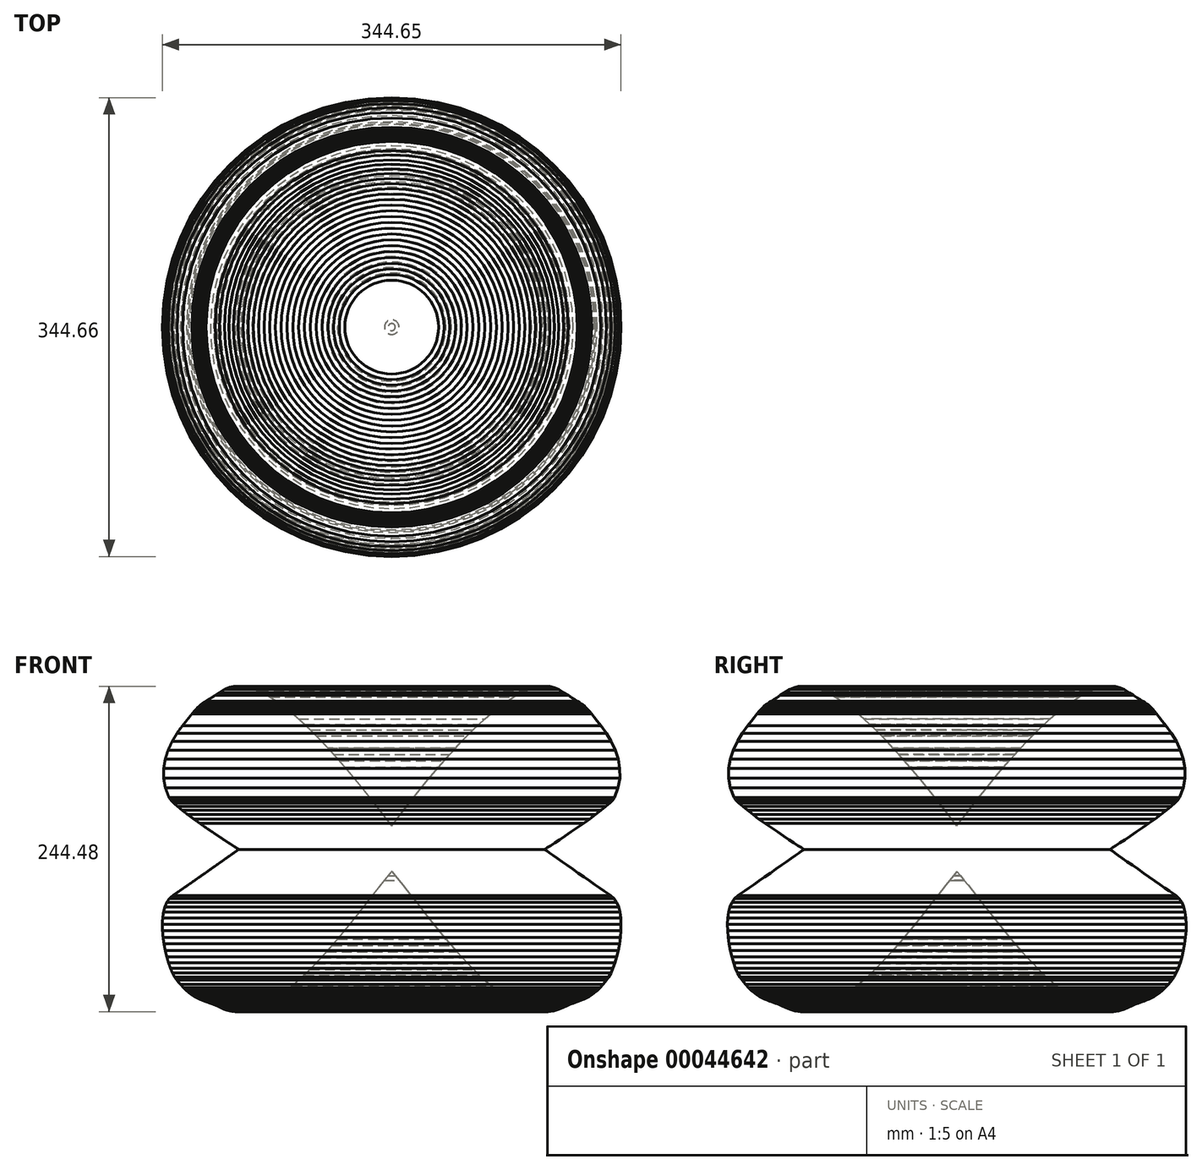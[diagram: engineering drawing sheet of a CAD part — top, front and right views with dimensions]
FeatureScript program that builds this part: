
annotation { "Feature Type Name" : "Feature", "Feature Type Description" : "" }
export const myFeature = defineFeature(function(context is Context, id is Id, definition is map)
    precondition{}
    {
        {
            var Q0;
            Q0=qCreatedBy(makeId("Front.planeOp"),FACE);
            var sketch = newSketch(context, id + "F0", { "sketchPlane" : qUnion([Q0])});
            skLineSegment(sketch, "E0", {"start": v(-86.16, 17.32) * mm, "end": v(-83.34, 21.03) * mm});
            skLineSegment(sketch, "E1", {"start": v(-83.34, 21.03) * mm, "end": v(-80.33, 24.97) * mm});
            skLineSegment(sketch, "E2", {"start": v(-80.33, 24.97) * mm, "end": v(-77.15, 29.11) * mm});
            skLineSegment(sketch, "E3", {"start": v(-77.15, 29.11) * mm, "end": v(-73.8, 33.43) * mm});
            skLineSegment(sketch, "E4", {"start": v(-73.8, 33.43) * mm, "end": v(-70.3, 37.9) * mm});
            skLineSegment(sketch, "E5", {"start": v(-70.3, 37.9) * mm, "end": v(-66.66, 42.47) * mm});
            skLineSegment(sketch, "E6", {"start": v(-66.66, 42.47) * mm, "end": v(-62.9, 47.16) * mm});
            skLineSegment(sketch, "E7", {"start": v(-62.9, 47.16) * mm, "end": v(-59, 51.9) * mm});
            skLineSegment(sketch, "E8", {"start": v(-59, 51.9) * mm, "end": v(-55.02, 56.7) * mm});
            skLineSegment(sketch, "E9", {"start": v(-55.02, 56.7) * mm, "end": v(-50.93, 61.52) * mm});
            skLineSegment(sketch, "E10", {"start": v(-50.93, 61.52) * mm, "end": v(-46.76, 66.33) * mm});
            skLineSegment(sketch, "E11", {"start": v(-46.76, 66.33) * mm, "end": v(-42.52, 71.1) * mm});
            skLineSegment(sketch, "E12", {"start": v(-42.52, 71.1) * mm, "end": v(-38.22, 75.82) * mm});
            skLineSegment(sketch, "E13", {"start": v(-38.22, 75.82) * mm, "end": v(-33.87, 80.45) * mm});
            skLineSegment(sketch, "E14", {"start": v(-33.87, 80.45) * mm, "end": v(-29.49, 84.97) * mm});
            skLineSegment(sketch, "E15", {"start": v(-29.49, 84.97) * mm, "end": v(-25.08, 89.36) * mm});
            skLineSegment(sketch, "E16", {"start": v(-25.08, 89.36) * mm, "end": v(-20.66, 93.58) * mm});
            skLineSegment(sketch, "E17", {"start": v(-20.66, 93.58) * mm, "end": v(-16.23, 97.62) * mm});
            skLineSegment(sketch, "E18", {"start": v(-16.23, 97.62) * mm, "end": v(-11.82, 101.44) * mm});
            skLineSegment(sketch, "E19", {"start": v(-11.82, 101.44) * mm, "end": v(-7.42, 105.03) * mm});
            skLineSegment(sketch, "E20", {"start": v(-7.42, 105.03) * mm, "end": v(-3.06, 108.35) * mm});
            skLineSegment(sketch, "E21", {"start": v(-3.06, 108.35) * mm, "end": v(1.26, 111.37) * mm});
            skLineSegment(sketch, "E22", {"start": v(1.26, 111.37) * mm, "end": v(5.52, 114.08) * mm});
            skLineSegment(sketch, "E23", {"start": v(5.52, 114.08) * mm, "end": v(9.71, 116.45) * mm});
            skLineSegment(sketch, "E24", {"start": v(9.71, 116.45) * mm, "end": v(13.83, 118.45) * mm});
            skLineSegment(sketch, "E25", {"start": v(13.83, 118.45) * mm, "end": v(17.85, 120.05) * mm});
            skLineSegment(sketch, "E26", {"start": v(17.85, 120.05) * mm, "end": v(21.77, 121.24) * mm});
            skLineSegment(sketch, "E27", {"start": v(21.77, 121.24) * mm, "end": v(25.58, 121.97) * mm});
            skLineSegment(sketch, "E28", {"start": v(25.58, 121.97) * mm, "end": v(29.27, 122.24) * mm});
            skLineSegment(sketch, "E29", {"start": v(29.27, 122.24) * mm, "end": v(32.81, 122) * mm});
            skLineSegment(sketch, "E30", {"start": v(32.81, 122) * mm, "end": v(36.21, 121.25) * mm});
            skLineSegment(sketch, "E31", {"start": v(36.21, 121.25) * mm, "end": v(39.45, 119.95) * mm});
            skLineSegment(sketch, "E32", {"start": v(39.45, 119.95) * mm, "end": v(43.29, 117.43) * mm});
            skLineSegment(sketch, "E33", {"start": v(43.29, 117.43) * mm, "end": v(46.52, 115.36) * mm});
            skLineSegment(sketch, "E34", {"start": v(46.52, 115.36) * mm, "end": v(49.22, 113.67) * mm});
            skLineSegment(sketch, "E35", {"start": v(49.22, 113.67) * mm, "end": v(51.47, 112.28) * mm});
            skLineSegment(sketch, "E36", {"start": v(51.47, 112.28) * mm, "end": v(53.35, 111.13) * mm});
            skLineSegment(sketch, "E37", {"start": v(53.35, 111.13) * mm, "end": v(54.92, 110.13) * mm});
            skLineSegment(sketch, "E38", {"start": v(54.92, 110.13) * mm, "end": v(56.28, 109.22) * mm});
            skLineSegment(sketch, "E39", {"start": v(56.28, 109.22) * mm, "end": v(57.48, 108.32) * mm});
            skLineSegment(sketch, "E40", {"start": v(57.48, 108.32) * mm, "end": v(58.62, 107.36) * mm});
            skLineSegment(sketch, "E41", {"start": v(58.62, 107.36) * mm, "end": v(59.76, 106.26) * mm});
            skLineSegment(sketch, "E42", {"start": v(59.76, 106.26) * mm, "end": v(60.98, 104.95) * mm});
            skLineSegment(sketch, "E43", {"start": v(60.98, 104.95) * mm, "end": v(62.36, 103.36) * mm});
            skLineSegment(sketch, "E44", {"start": v(62.36, 103.36) * mm, "end": v(63.98, 101.4) * mm});
            skLineSegment(sketch, "E45", {"start": v(63.98, 101.4) * mm, "end": v(65.9, 99.03) * mm});
            skLineSegment(sketch, "E46", {"start": v(65.9, 99.03) * mm, "end": v(68.21, 96.15) * mm});
            skLineSegment(sketch, "E47", {"start": v(68.21, 96.15) * mm, "end": v(71, 92.69) * mm});
            skLineSegment(sketch, "E48", {"start": v(71, 92.69) * mm, "end": v(75.17, 87) * mm});
            skLineSegment(sketch, "E49", {"start": v(75.17, 87) * mm, "end": v(78.84, 80.83) * mm});
            skLineSegment(sketch, "E50", {"start": v(78.84, 80.83) * mm, "end": v(81.85, 74.28) * mm});
            skLineSegment(sketch, "E51", {"start": v(81.85, 74.28) * mm, "end": v(84.03, 67.44) * mm});
            skLineSegment(sketch, "E52", {"start": v(84.03, 67.44) * mm, "end": v(85.21, 60.37) * mm});
            skLineSegment(sketch, "E53", {"start": v(85.21, 60.37) * mm, "end": v(85.24, 53.17) * mm});
            skLineSegment(sketch, "E54", {"start": v(85.24, 53.17) * mm, "end": v(83.94, 45.92) * mm});
            skLineSegment(sketch, "E55", {"start": v(83.94, 45.92) * mm, "end": v(81.15, 38.7) * mm});
            skLineSegment(sketch, "E56", {"start": v(81.15, 38.7) * mm, "end": v(79.84, 36.83) * mm});
            skLineSegment(sketch, "E57", {"start": v(79.84, 36.83) * mm, "end": v(77.65, 34.52) * mm});
            skLineSegment(sketch, "E58", {"start": v(77.65, 34.52) * mm, "end": v(74.7, 31.86) * mm});
            skLineSegment(sketch, "E59", {"start": v(74.7, 31.86) * mm, "end": v(71.12, 28.93) * mm});
            skLineSegment(sketch, "E60", {"start": v(71.12, 28.93) * mm, "end": v(67.07, 25.79) * mm});
            skLineSegment(sketch, "E61", {"start": v(67.07, 25.79) * mm, "end": v(62.66, 22.53) * mm});
            skLineSegment(sketch, "E62", {"start": v(62.66, 22.53) * mm, "end": v(58.03, 19.21) * mm});
            skLineSegment(sketch, "E63", {"start": v(58.03, 19.21) * mm, "end": v(53.32, 15.92) * mm});
            skLineSegment(sketch, "E64", {"start": v(53.32, 15.92) * mm, "end": v(48.66, 12.74) * mm});
            skLineSegment(sketch, "E65", {"start": v(48.66, 12.74) * mm, "end": v(44.19, 9.73) * mm});
            skLineSegment(sketch, "E66", {"start": v(44.19, 9.73) * mm, "end": v(40.03, 6.97) * mm});
            skLineSegment(sketch, "E67", {"start": v(40.03, 6.97) * mm, "end": v(36.33, 4.55) * mm});
            skLineSegment(sketch, "E68", {"start": v(36.33, 4.55) * mm, "end": v(33.22, 2.53) * mm});
            skLineSegment(sketch, "E69", {"start": v(33.22, 2.53) * mm, "end": v(30.83, 1) * mm});
            skLineSegment(sketch, "E70", {"start": v(30.83, 1) * mm, "end": v(29.3, 0.02) * mm});
            skLineSegment(sketch, "E71", {"start": v(29.3, 0.02) * mm, "end": v(28.76, -0.32) * mm});
            skLineSegment(sketch, "E72", {"start": v(28.76, -0.32) * mm, "end": v(29.2, -0.64) * mm});
            skLineSegment(sketch, "E73", {"start": v(29.2, -0.64) * mm, "end": v(30.48, -1.54) * mm});
            skLineSegment(sketch, "E74", {"start": v(30.48, -1.54) * mm, "end": v(32.48, -2.95) * mm});
            skLineSegment(sketch, "E75", {"start": v(32.48, -2.95) * mm, "end": v(35.1, -4.8) * mm});
            skLineSegment(sketch, "E76", {"start": v(35.1, -4.8) * mm, "end": v(38.26, -7.03) * mm});
            skLineSegment(sketch, "E77", {"start": v(38.26, -7.03) * mm, "end": v(41.83, -9.55) * mm});
            skLineSegment(sketch, "E78", {"start": v(41.83, -9.55) * mm, "end": v(45.72, -12.3) * mm});
            skLineSegment(sketch, "E79", {"start": v(45.72, -12.3) * mm, "end": v(49.83, -15.18) * mm});
            skLineSegment(sketch, "E80", {"start": v(49.83, -15.18) * mm, "end": v(54.06, -18.16) * mm});
            skLineSegment(sketch, "E81", {"start": v(54.06, -18.16) * mm, "end": v(58.3, -21.13) * mm});
            skLineSegment(sketch, "E82", {"start": v(58.3, -21.13) * mm, "end": v(62.47, -24.04) * mm});
            skLineSegment(sketch, "E83", {"start": v(62.47, -24.04) * mm, "end": v(66.44, -26.82) * mm});
            skLineSegment(sketch, "E84", {"start": v(66.44, -26.82) * mm, "end": v(70.13, -29.38) * mm});
            skLineSegment(sketch, "E85", {"start": v(70.13, -29.38) * mm, "end": v(73.44, -31.65) * mm});
            skLineSegment(sketch, "E86", {"start": v(73.44, -31.65) * mm, "end": v(76.25, -33.57) * mm});
            skLineSegment(sketch, "E87", {"start": v(76.25, -33.57) * mm, "end": v(78.47, -35.07) * mm});
            skLineSegment(sketch, "E88", {"start": v(78.47, -35.07) * mm, "end": v(80.92, -37.24) * mm});
            skLineSegment(sketch, "E89", {"start": v(80.92, -37.24) * mm, "end": v(82.85, -40.1) * mm});
            skLineSegment(sketch, "E90", {"start": v(82.85, -40.1) * mm, "end": v(84.3, -43.55) * mm});
            skLineSegment(sketch, "E91", {"start": v(84.3, -43.55) * mm, "end": v(85.32, -47.5) * mm});
            skLineSegment(sketch, "E92", {"start": v(85.32, -47.5) * mm, "end": v(85.93, -51.85) * mm});
            skLineSegment(sketch, "E93", {"start": v(85.93, -51.85) * mm, "end": v(86.16, -56.5) * mm});
            skLineSegment(sketch, "E94", {"start": v(86.16, -56.5) * mm, "end": v(86.06, -61.37) * mm});
            skLineSegment(sketch, "E95", {"start": v(86.06, -61.37) * mm, "end": v(85.64, -66.35) * mm});
            skLineSegment(sketch, "E96", {"start": v(85.64, -66.35) * mm, "end": v(84.95, -71.34) * mm});
            skLineSegment(sketch, "E97", {"start": v(84.95, -71.34) * mm, "end": v(84.02, -76.26) * mm});
            skLineSegment(sketch, "E98", {"start": v(84.02, -76.26) * mm, "end": v(82.88, -81) * mm});
            skLineSegment(sketch, "E99", {"start": v(82.88, -81) * mm, "end": v(81.57, -85.46) * mm});
            skLineSegment(sketch, "E100", {"start": v(81.57, -85.46) * mm, "end": v(80.12, -89.56) * mm});
            skLineSegment(sketch, "E101", {"start": v(80.12, -89.56) * mm, "end": v(78.56, -93.2) * mm});
            skLineSegment(sketch, "E102", {"start": v(78.56, -93.2) * mm, "end": v(76.93, -96.26) * mm});
            skLineSegment(sketch, "E103", {"start": v(76.93, -96.26) * mm, "end": v(75.27, -98.68) * mm});
            skLineSegment(sketch, "E104", {"start": v(75.27, -98.68) * mm, "end": v(72.72, -101.67) * mm});
            skLineSegment(sketch, "E105", {"start": v(72.72, -101.67) * mm, "end": v(70.36, -104.22) * mm});
            skLineSegment(sketch, "E106", {"start": v(70.36, -104.22) * mm, "end": v(68.16, -106.36) * mm});
            skLineSegment(sketch, "E107", {"start": v(68.16, -106.36) * mm, "end": v(66.07, -108.15) * mm});
            skLineSegment(sketch, "E108", {"start": v(66.07, -108.15) * mm, "end": v(64.08, -109.65) * mm});
            skLineSegment(sketch, "E109", {"start": v(64.08, -109.65) * mm, "end": v(62.14, -110.89) * mm});
            skLineSegment(sketch, "E110", {"start": v(62.14, -110.89) * mm, "end": v(60.24, -111.93) * mm});
            skLineSegment(sketch, "E111", {"start": v(60.24, -111.93) * mm, "end": v(58.34, -112.82) * mm});
            skLineSegment(sketch, "E112", {"start": v(58.34, -112.82) * mm, "end": v(56.4, -113.6) * mm});
            skLineSegment(sketch, "E113", {"start": v(56.4, -113.6) * mm, "end": v(54.4, -114.35) * mm});
            skLineSegment(sketch, "E114", {"start": v(54.4, -114.35) * mm, "end": v(52.32, -115.1) * mm});
            skLineSegment(sketch, "E115", {"start": v(52.32, -115.1) * mm, "end": v(50.11, -115.9) * mm});
            skLineSegment(sketch, "E116", {"start": v(50.11, -115.9) * mm, "end": v(47.75, -116.79) * mm});
            skLineSegment(sketch, "E117", {"start": v(47.75, -116.79) * mm, "end": v(45.21, -117.84) * mm});
            skLineSegment(sketch, "E118", {"start": v(45.21, -117.84) * mm, "end": v(42.45, -119.1) * mm});
            skLineSegment(sketch, "E119", {"start": v(42.45, -119.1) * mm, "end": v(39.45, -120.6) * mm});
            skLineSegment(sketch, "E120", {"start": v(39.45, -120.6) * mm, "end": v(35.47, -121.7) * mm});
            skLineSegment(sketch, "E121", {"start": v(35.47, -121.7) * mm, "end": v(31.42, -122.24) * mm});
            skLineSegment(sketch, "E122", {"start": v(31.42, -122.24) * mm, "end": v(27.3, -122.24) * mm});
            skLineSegment(sketch, "E123", {"start": v(27.3, -122.24) * mm, "end": v(23.12, -121.73) * mm});
            skLineSegment(sketch, "E124", {"start": v(23.12, -121.73) * mm, "end": v(18.89, -120.74) * mm});
            skLineSegment(sketch, "E125", {"start": v(18.89, -120.74) * mm, "end": v(14.61, -119.3) * mm});
            skLineSegment(sketch, "E126", {"start": v(14.61, -119.3) * mm, "end": v(10.3, -117.44) * mm});
            skLineSegment(sketch, "E127", {"start": v(10.3, -117.44) * mm, "end": v(5.96, -115.18) * mm});
            skLineSegment(sketch, "E128", {"start": v(5.96, -115.18) * mm, "end": v(1.6, -112.55) * mm});
            skLineSegment(sketch, "E129", {"start": v(1.6, -112.55) * mm, "end": v(-2.77, -109.59) * mm});
            skLineSegment(sketch, "E130", {"start": v(-2.77, -109.59) * mm, "end": v(-7.15, -106.32) * mm});
            skLineSegment(sketch, "E131", {"start": v(-7.15, -106.32) * mm, "end": v(-11.53, -102.76) * mm});
            skLineSegment(sketch, "E132", {"start": v(-11.53, -102.76) * mm, "end": v(-15.89, -98.96) * mm});
            skLineSegment(sketch, "E133", {"start": v(-15.89, -98.96) * mm, "end": v(-20.23, -94.93) * mm});
            skLineSegment(sketch, "E134", {"start": v(-20.23, -94.93) * mm, "end": v(-24.55, -90.71) * mm});
            skLineSegment(sketch, "E135", {"start": v(-24.55, -90.71) * mm, "end": v(-28.83, -86.32) * mm});
            skLineSegment(sketch, "E136", {"start": v(-28.83, -86.32) * mm, "end": v(-33.07, -81.8) * mm});
            skLineSegment(sketch, "E137", {"start": v(-33.07, -81.8) * mm, "end": v(-37.26, -77.17) * mm});
            skLineSegment(sketch, "E138", {"start": v(-37.26, -77.17) * mm, "end": v(-41.39, -72.45) * mm});
            skLineSegment(sketch, "E139", {"start": v(-41.39, -72.45) * mm, "end": v(-45.45, -67.69) * mm});
            skLineSegment(sketch, "E140", {"start": v(-45.45, -67.69) * mm, "end": v(-49.44, -62.9) * mm});
            skLineSegment(sketch, "E141", {"start": v(-49.44, -62.9) * mm, "end": v(-53.35, -58.12) * mm});
            skLineSegment(sketch, "E142", {"start": v(-53.35, -58.12) * mm, "end": v(-57.16, -53.37) * mm});
            skLineSegment(sketch, "E143", {"start": v(-57.16, -53.37) * mm, "end": v(-60.88, -48.68) * mm});
            skLineSegment(sketch, "E144", {"start": v(-60.88, -48.68) * mm, "end": v(-64.5, -44.09) * mm});
            skLineSegment(sketch, "E145", {"start": v(-64.5, -44.09) * mm, "end": v(-68, -39.61) * mm});
            skLineSegment(sketch, "E146", {"start": v(-68, -39.61) * mm, "end": v(-71.37, -35.29) * mm});
            skLineSegment(sketch, "E147", {"start": v(-71.37, -35.29) * mm, "end": v(-74.62, -31.14) * mm});
            skLineSegment(sketch, "E148", {"start": v(-74.62, -31.14) * mm, "end": v(-77.73, -27.2) * mm});
            skLineSegment(sketch, "E149", {"start": v(-77.73, -27.2) * mm, "end": v(-80.7, -23.5) * mm});
            skLineSegment(sketch, "E150", {"start": v(-80.7, -23.5) * mm, "end": v(-83.51, -20.05) * mm});
            skLineSegment(sketch, "E151", {"start": v(-83.51, -20.05) * mm, "end": v(-86.16, -16.9) * mm});
            skLineSegment(sketch, "E152", {"start": v(-86.16, -16.9) * mm, "end": v(-86.16, 17.32) * mm});
            skSolve(sketch);
        }
        {
            var Q0;
            Q0=makeQuery(id+"F0.imprint","IMPRINT",FACE,{"disambiguationData":[TD([[makeQuery(id+"F0.imprint","IMPRINT",EDGE,{"derivedFrom":sQuery(id+"F0.wireOp",EDGE,"E0")}),-1.0]])]});
            var Q1;
            Q1=sQuery(id+"F0.wireOp",EDGE,"E152");
            revolve(context, id + "F1", {"entities" : qUnion([Q0]), "axis" : qUnion([Q1]), "revolveType" : RevolveType.FULL});
        }
    });
